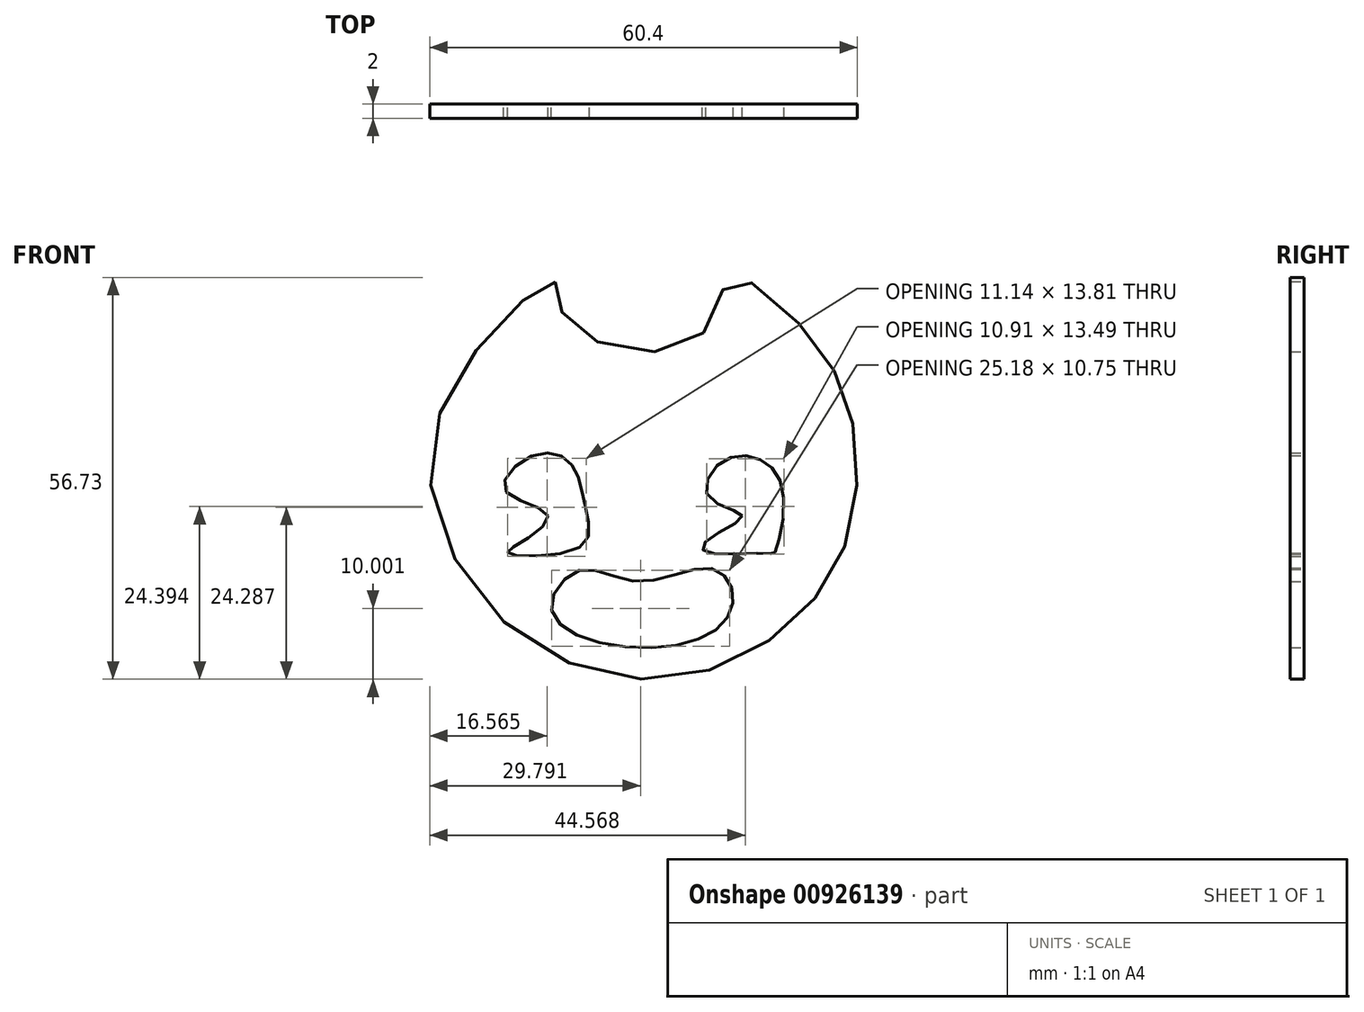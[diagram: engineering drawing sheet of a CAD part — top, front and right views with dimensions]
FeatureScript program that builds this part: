
annotation { "Feature Type Name" : "Feature", "Feature Type Description" : "" }
export const myFeature = defineFeature(function(context is Context, id is Id, definition is map)
    precondition{}
    {
        {
            var Q0;
            Q0=qCreatedBy(makeId("Front.planeOp"),FACE);
            var sketch = newSketch(context, id + "F0", { "sketchPlane" : qUnion([Q0])});
            skFitSpline(sketch, "E0", {"points": [v(-49.55, 64.08) * mm, v(-48.76, 60.12) * mm, v(-40.04, 54.57) * mm, v(-28.14, 57.48) * mm, v(-24.7, 64.61) * mm, v(-14.67, 57.74) * mm, v(-7.8, 45.32) * mm, v(-8.06, 28.67) * mm, v(-16.78, 15.46) * mm, v(-34.49, 8.06) * mm, v(-56.68, 15.99) * mm, v(-67.25, 39.24) * mm, v(-56.95, 58.8) * mm, v(-49.55, 64.08) * mm]});
            skSolve(sketch);
        }
        {
            var Q0;
            Q0=makeQuery(id+"F0.imprint","IMPRINT",FACE,{"disambiguationData":[TD([[makeQuery(id+"F0.imprint","IMPRINT",EDGE,{"derivedFrom":sQuery(id+"F0.wireOp",EDGE,"E0")}),-1.0]])]});
            extrude(context, id + "F1", {"entities" : qUnion([Q0]), "depth" : 2 * mm, "offsetDistance" : 25 * mm});
        }
        {
            var Q0;
            Q0=makeQuery(id+"F1.opExtrude","CAP_FACE",FACE,{"disambiguationData":[OSD([sQuery(id+"F0.wireOp",EDGE,"E0")])],"isStart":false});
            var sketch = newSketch(context, id + "F2", { "sketchPlane" : qUnion([Q0])});
            skFitSpline(sketch, "E1", {"points": [v(-50.6, 31.05) * mm, v(-56.68, 34.75) * mm, v(-52.2, 39.77) * mm, v(-47.17, 38.19) * mm, v(-45.32, 32.37) * mm, v(-45.85, 26.82) * mm, v(-56.16, 25.77) * mm, v(-55.63, 26.56) * mm, v(-50.6, 31.05) * mm]});
            skFitSpline(sketch, "E2", {"points": [v(-23.12, 31.05) * mm, v(-27.88, 33.7) * mm, v(-26.03, 38.71) * mm, v(-20.48, 38.98) * mm, v(-17.3, 33.96) * mm, v(-18.63, 25.77) * mm, v(-19.42, 25.77) * mm, v(-28.4, 26.03) * mm, v(-28.14, 27.62) * mm, v(-23.12, 31.05) * mm]});
            skSolve(sketch);
        }
        {
            var Q0;
            Q0=makeQuery(id+"F2.imprint","IMPRINT",FACE,{"disambiguationData":[TD([[makeQuery(id+"F2.imprint","IMPRINT",EDGE,{"derivedFrom":sQuery(id+"F2.wireOp",EDGE,"E1")}),-1.0]])]});
            var Q1;
            Q1=makeQuery(id+"F2.imprint","IMPRINT",FACE,{"disambiguationData":[TD([[makeQuery(id+"F2.imprint","IMPRINT",EDGE,{"derivedFrom":sQuery(id+"F2.wireOp",EDGE,"E2")}),-1.0]])]});
            extrude(context, id + "F3", {"entities" : qUnion([Q0, Q1]), "operationType" : NewBodyOperationType.REMOVE, "oppositeDirection" : true, "depth" : 25 * mm, "offsetDistance" : 25 * mm});
        }
        {
            var Q0;
            Q0=makeQuery(id+"F1.opExtrude","CAP_FACE",FACE,{"disambiguationData":[OSD([sQuery(id+"F0.wireOp",EDGE,"E0")])],"isStart":false});
            var sketch = newSketch(context, id + "F4", { "sketchPlane" : qUnion([Q0])});
            skFitSpline(sketch, "E3", {"points": [v(-46.11, 23.39) * mm, v(-37.66, 21.8) * mm, v(-27.62, 23.65) * mm, v(-24.44, 19.95) * mm, v(-27.35, 14.67) * mm, v(-41.36, 12.82) * mm, v(-50.08, 17.84) * mm, v(-46.11, 23.39) * mm]});
            skSolve(sketch);
        }
        {
            var Q0;
            Q0=makeQuery(id+"F4.imprint","IMPRINT",FACE,{"disambiguationData":[TD([[makeQuery(id+"F4.imprint","IMPRINT",EDGE,{"derivedFrom":sQuery(id+"F4.wireOp",EDGE,"E3")}),-1.0]])]});
            extrude(context, id + "F5", {"entities" : qUnion([Q0]), "operationType" : NewBodyOperationType.REMOVE, "oppositeDirection" : true, "depth" : 25 * mm, "offsetDistance" : 25 * mm});
        }
    });
